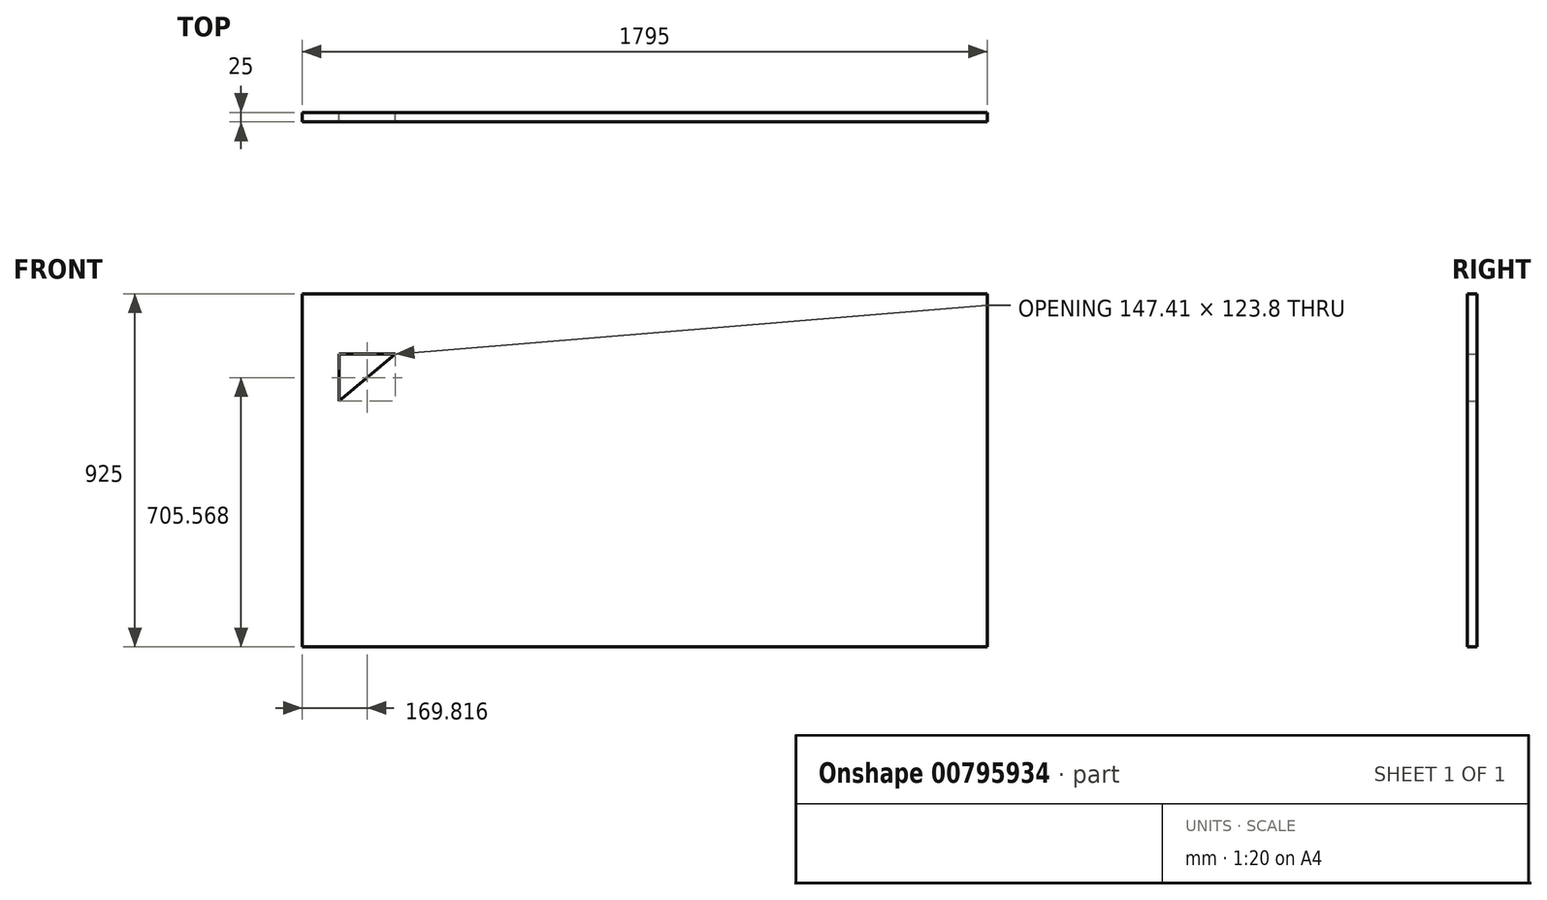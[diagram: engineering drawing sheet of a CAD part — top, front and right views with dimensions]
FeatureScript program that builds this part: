
annotation { "Feature Type Name" : "Feature", "Feature Type Description" : "" }
export const myFeature = defineFeature(function(context is Context, id is Id, definition is map)
    precondition{}
    {
        {
            var Q0;
            Q0=qCreatedBy(makeId("Front.planeOp"),FACE);
            var sketch = newSketch(context, id + "F0", { "sketchPlane" : qUnion([Q0])});
            skLineSegment(sketch, "E0.bottom", {"start": v(-897.5, 462.5) * mm, "end": v(897.5, 462.5) * mm});
            skLineSegment(sketch, "E0.top", {"start": v(-897.5, -462.5) * mm, "end": v(897.5, -462.5) * mm});
            skLineSegment(sketch, "E0.left", {"start": v(-897.5, 462.5) * mm, "end": v(-897.5, -462.5) * mm});
            skLineSegment(sketch, "E0.right", {"start": v(897.5, 462.5) * mm, "end": v(897.5, -462.5) * mm});
            skPoint(sketch, "E0.middle", {"position": v(0, 0) * mm});
            skSolve(sketch);
        }
        {
            var Q0;
            Q0 = qSketchRegion(id + "F0", true);
            extrude(context, id + "F1", {"entities" : qUnion([Q0]), "depth" : 25 * mm, "offsetDistance" : 25 * mm});
        }
        {
            var Q0;
            Q0=makeQuery(id+"F1.opExtrude","CAP_FACE",FACE,{"disambiguationData":[OSD([sQuery(id+"F0.wireOp",EDGE,"E0.bottom"),sQuery(id+"F0.wireOp",EDGE,"E0.top"),sQuery(id+"F0.wireOp",EDGE,"E0.left"),sQuery(id+"F0.wireOp",EDGE,"E0.right")])],"isStart":true});
            var sketch = newSketch(context, id + "F2", { "sketchPlane" : qUnion([Q0])});
            skLineSegment(sketch, "E1", {"start": v(653.98, 304.97) * mm, "end": v(801.39, 304.97) * mm});
            skLineSegment(sketch, "E2", {"start": v(801.39, 304.97) * mm, "end": v(801.39, 181.17) * mm});
            skLineSegment(sketch, "E3", {"start": v(801.39, 181.17) * mm, "end": v(653.98, 304.97) * mm});
            skSolve(sketch);
        }
        {
            var Q0;
            Q0 = qSketchRegion(id + "F2", true);
            extrude(context, id + "F3", {"entities" : qUnion([Q0]), "operationType" : NewBodyOperationType.REMOVE, "endBound" : BoundingType.UP_TO_NEXT, "oppositeDirection" : true, "depth" : 25 * mm, "offsetDistance" : 25 * mm});
        }
    });
